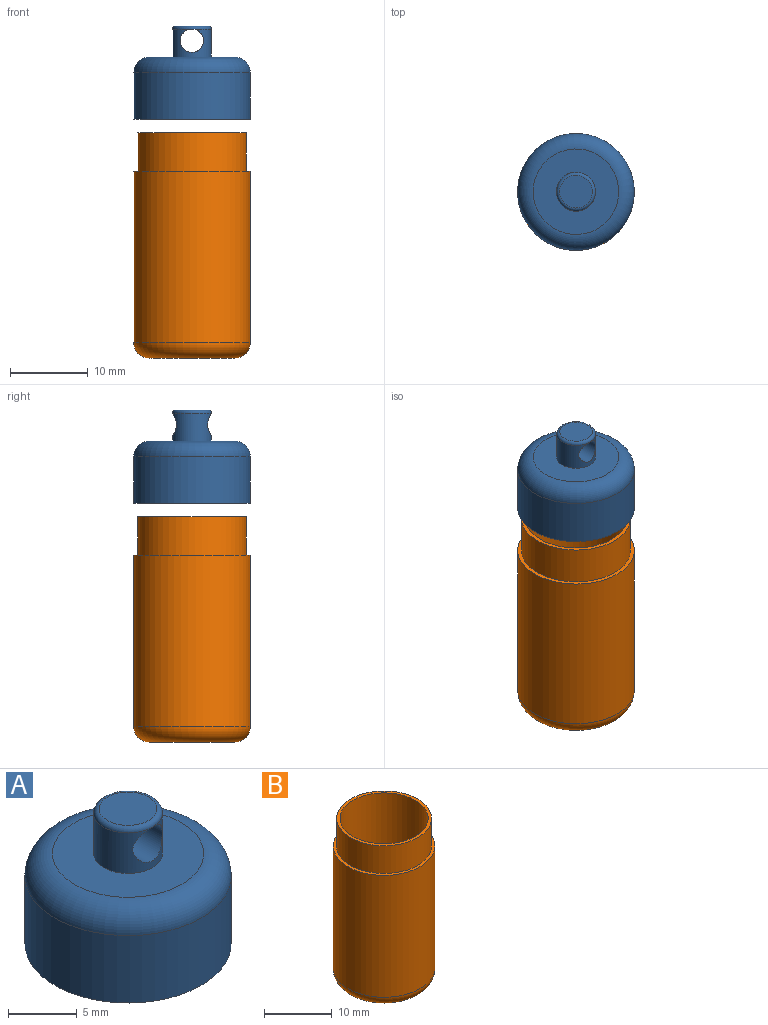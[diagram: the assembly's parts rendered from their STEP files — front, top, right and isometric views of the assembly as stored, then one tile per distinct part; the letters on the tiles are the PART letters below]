
ASSEMBLY  parts=2 mates=1
PART A: 12 faces, bbox 16.2x16.2x12 mm
  f0: cylinder r=7.5mm len=15mm, axis (0,0,-1), area 282.7mm2, adj f2,f3
  f1: plane 11x11mm, normal (0,0,1), area 75.4mm2, adj f3,f4
  f2: plane 15x15mm, normal (0,0,-1), area 22.8mm2, adj f0,f8
  f3: torus R=5.5mm, axis (0,0,1), area 133.7mm2, adj f0,f1
  f4: cylinder r=2.5mm len=5mm, axis (0,0,-1), area 41.7mm2, adj f1,f6,f7
  f5: plane 4.2x4.2mm, normal (0,0,1), area 13.9mm2, adj f7
  f6: cylinder r=1.5mm len=5mm, axis (0,-1,0), area 42.5mm2, adj f4,f7
  f7: torus R=2.1mm, axis (0,0,1), area 9.3mm2, adj f4,f5,f6
  f8: cylinder r=7mm len=14mm, axis (0,0,-1), area 219.9mm2, adj f2,f9
  f9: plane 14x14mm, normal (0,0,-1), area 21.2mm2, adj f8,f11
  f10: plane 13x13mm, normal (0,0,-1), area 132.7mm2, adj f11
  f11: cylinder r=6.5mm len=13mm, axis (0,0,-1), area 81.7mm2, adj f9,f10
PART B: 9 faces, bbox 16.2x16.2x29 mm
  f0: plane 14x14mm, normal (0,0,1), area 21.2mm2, adj f1,f4
  f1: cylinder r=6.5mm len=27mm, axis (0,0,-1), area 1102.7mm2, adj f0,f3
  f2: plane 11x11mm, normal (0,0,1), area 95mm2, adj f3
  f3: torus R=5.5mm, axis (0,0,1), area 60.6mm2, adj f1,f2
  f4: cylinder r=7mm len=14mm, axis (0,0,-1), area 219.9mm2, adj f0,f5
  f5: plane 15x15mm, normal (0,0,1), area 22.8mm2, adj f4,f8
  f6: plane 11x11mm, normal (0,0,-1), area 95mm2, adj f7
  f7: torus R=5.5mm, axis (0,0,1), area 133.7mm2, adj f6,f8
  f8: cylinder r=7.5mm len=22mm, axis (0,0,-1), area 1036.7mm2, adj f5,f7
PLACE A t=(-8.76,3.41,-0.84)mm
PLACE B t=(-8.76,3.41,-7.54)mm
MATE slider A.f8 <-> B.f4  axis (0,0,-1) through (-8.76,3.41,23.16)mm
